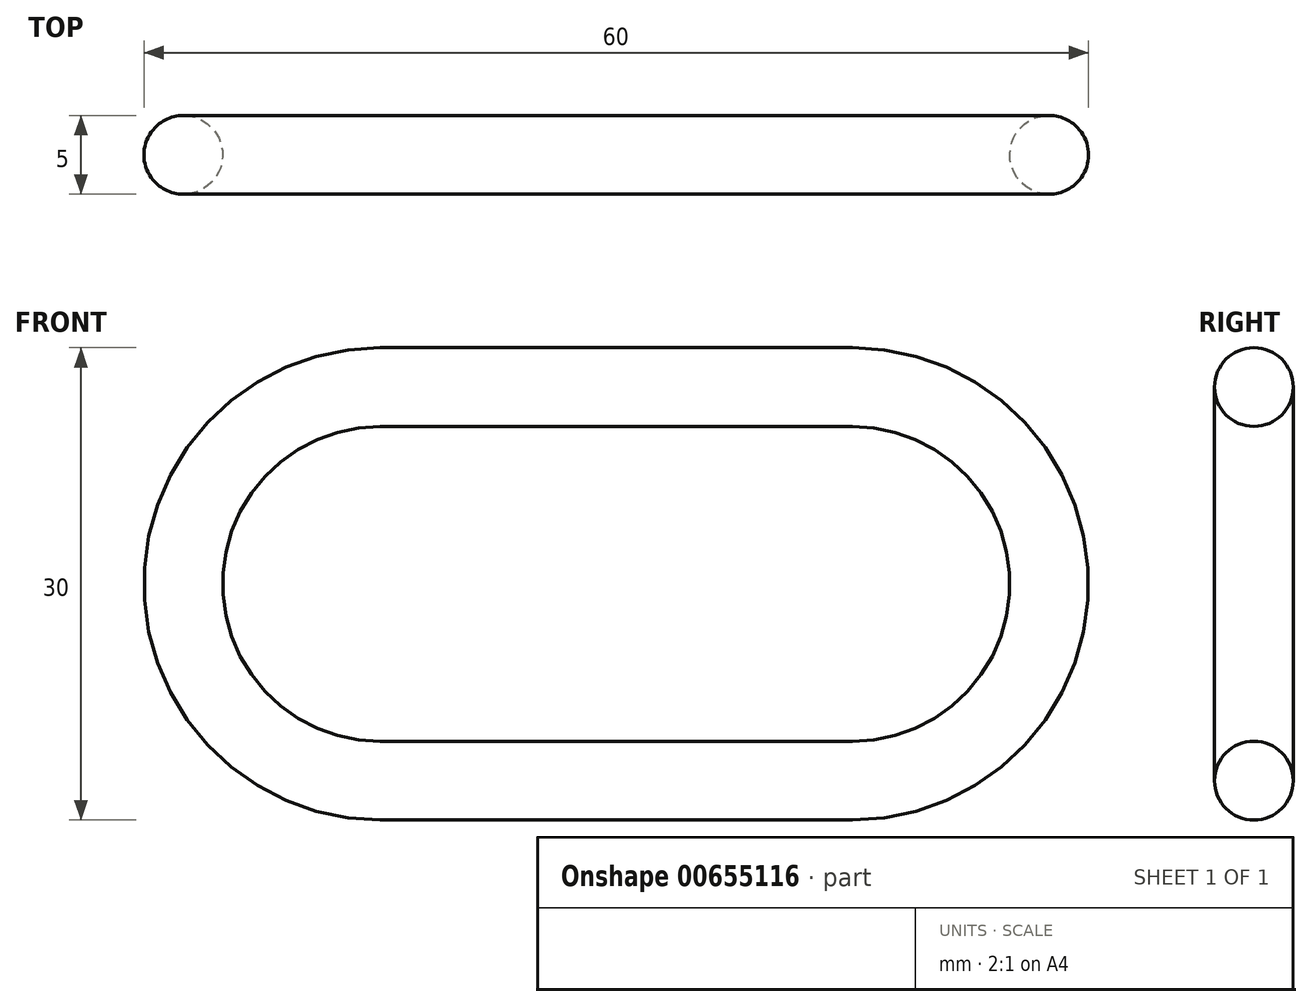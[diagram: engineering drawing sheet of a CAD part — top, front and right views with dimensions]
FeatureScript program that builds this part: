
annotation { "Feature Type Name" : "Feature", "Feature Type Description" : "" }
export const myFeature = defineFeature(function(context is Context, id is Id, definition is map)
    precondition{}
    {
        {
            var Q0;
            Q0=qCreatedBy(makeId("Front.planeOp"),FACE);
            var sketch = newSketch(context, id + "F0", { "sketchPlane" : qUnion([Q0])});
            skLineSegment(sketch, "E0.bottom", {"start": v(15, -10) * mm, "end": v(-15, -10) * mm});
            skLineSegment(sketch, "E0.top", {"start": v(15, 10) * mm, "end": v(-15, 10) * mm});
            skLineSegment(sketch, "E0.left", {"start": v(25, 0) * mm, "end": v(25, 0) * mm});
            skLineSegment(sketch, "E0.right", {"start": v(-25, 0) * mm, "end": v(-25, 0) * mm});
            skPoint(sketch, "E0.middle", {"position": v(0, 0) * mm});
            skPoint(sketch, "E1.visualSharp", {"position": v(-25, 10) * mm});
            skArc(sketch, "E1.filletArc", {"start": v(-15, 10) * mm, "mid": v(-22.07, 7.07) * mm, "end": v(-25, 0) * mm});
            skPoint(sketch, "E2.visualSharp", {"position": v(25, 10) * mm});
            skArc(sketch, "E2.filletArc", {"start": v(25, 0) * mm, "mid": v(22.07, 7.07) * mm, "end": v(15, 10) * mm});
            skPoint(sketch, "E3.visualSharp", {"position": v(25, -10) * mm});
            skArc(sketch, "E3.filletArc", {"start": v(15, -10) * mm, "mid": v(22.07, -7.07) * mm, "end": v(25, 0) * mm});
            skPoint(sketch, "E4.visualSharp", {"position": v(-25, -10) * mm});
            skArc(sketch, "E4.filletArc", {"start": v(-25, 0) * mm, "mid": v(-22.07, -7.07) * mm, "end": v(-15, -10) * mm});
            skArc(sketch, "E5.0", {"start": v(30, 0) * mm, "mid": v(25.6, 10.6) * mm, "end": v(15, 15) * mm});
            skArc(sketch, "E5.1", {"start": v(-15, 15) * mm, "mid": v(-25.6, 10.6) * mm, "end": v(-30, 0) * mm});
            skArc(sketch, "E5.2", {"start": v(-30, 0) * mm, "mid": v(-25.6, -10.6) * mm, "end": v(-15, -15) * mm});
            skLineSegment(sketch, "E5.3", {"start": v(15, 15) * mm, "end": v(-15, 15) * mm});
            skLineSegment(sketch, "E5.4", {"start": v(15, -15) * mm, "end": v(-15, -15) * mm});
            skArc(sketch, "E5.5", {"start": v(15, -15) * mm, "mid": v(25.6, -10.6) * mm, "end": v(30, 0) * mm});
            skSolve(sketch);
        }
        {
            var Q0;
            Q0=makeQuery(id+"F0.imprint","IMPRINT",FACE,{"disambiguationData":[TD([[makeQuery(id+"F0.imprint","IMPRINT",EDGE,{"derivedFrom":sQuery(id+"F0.wireOp",EDGE,"E0.bottom")}),1.0]])]});
            extrude(context, id + "F1", {"entities" : qUnion([Q0]), "depth" : 2.5 * mm, "offsetDistance" : 25 * mm, "hasSecondDirection" : true, "secondDirectionOppositeDirection" : true, "secondDirectionDepth" : 2.5 * mm});
        }
        {
            var Q0;
            Q0=makeQuery(id+"F1.opExtrude","CAP_EDGE",EDGE,{"disambiguationData":[OSD([sQuery(id+"F0.wireOp",EDGE,"E5.4")])],"isStart":false});
            var Q1;
            Q1=makeQuery(id+"F1.opExtrude","CAP_EDGE",EDGE,{"disambiguationData":[OSD([sQuery(id+"F0.wireOp",EDGE,"E5.4")])],"isStart":true});
            var Q2;
            Q2=makeQuery(id+"F1.opExtrude","CAP_EDGE",EDGE,{"disambiguationData":[OSD([sQuery(id+"F0.wireOp",EDGE,"E0.bottom")])],"isStart":false});
            var Q3;
            Q3=makeQuery(id+"F1.opExtrude","CAP_EDGE",EDGE,{"disambiguationData":[OSD([sQuery(id+"F0.wireOp",EDGE,"E0.bottom")])],"isStart":true});
            fillet(context, id + "F2", {"entities" : qUnion([Q0, Q1, Q2, Q3]), "radius" : 2.5 * mm, "tangentPropagation" : true, "allowEdgeOverflow" : false});
        }
    });
